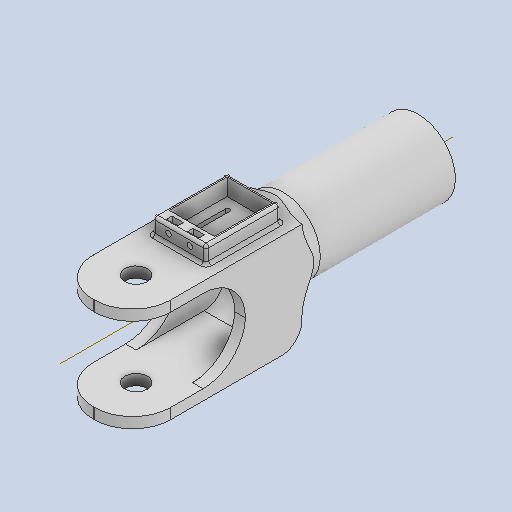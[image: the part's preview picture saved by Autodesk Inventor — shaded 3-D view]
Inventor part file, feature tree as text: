
AUTODESK INVENTOR PART (.ipt)
format: ipt  version: 2024 (Build 280153000, 153)  size: 337,920 bytes
history: native  units: mm
features: extrude x10, fillet x7, sketch x3, shell x1
ambient origin geometry x8: Origin, YZ Plane, XZ Plane, XY Plane, X Axis, Y Axis, Z Axis, Center Point
bodies: Solid1 (feature_tree)
feature tree (21):
  extrude  "Extrusion1"  Depth=30.0mm TaperAngle=0.0deg
  extrude  "Extrusion2"  Depth=47.5mm
  extrude  "Extrusion3"  Depth=14.25mm
  shell  "Shell1"  Thickness=80.0mm
  extrude  "Extrusion4"  Depth=14.25mm
  fillet  "Fillet2"  Radius=7.5mm
  extrude  "Extrusion5"  Depth=14.25mm
  fillet  "Fillet5"  Radius=80.0mm
  extrude  "Extrusion6"  Depth=14.25mm TaperAngle=0.0deg
  extrude  "Extrusion8"  Depth=14.25mm
  fillet  "Fillet6"  Radius=80.0mm
  extrude  "Extrusion9"  Depth=14.25mm
  extrude  "Extrusion10"  Depth=14.25mm
  extrude  "Extrusion11"  Depth=14.25mm
  fillet  "Fillet7"  Radius=46.0mm
  fillet  "Fillet8"  Radius=30.0mm
  fillet  "Fillet9"  Radius=55.0mm
  fillet  "Fillet10"  Radius=30.0mm
  sketch  "Sketch1"  dims[d1=52.629mm d2=30.0mm d3=0.0mm]
  sketch  "Sketch5"  dims[d6=47.5mm d7=47.5mm]
  sketch  "Sketch10"  dims[d9=120.0mm d10=0.0mm d12=52.629mm d13=80.0mm d14=0.0mm d15=7.5mm d16=7.5mm d17=7.5mm d18=80.0mm d19=80.0mm d20=0.0mm d21=27.0mm d22=80.0mm d23=0.0mm d24=55.0mm d25=27.5mm d26=27.5mm d27=46.0mm d30=30.0mm d31=55.0mm d32=30.0mm d33=16.0mm d34=0.0mm d35=0.0mm d41=3.0mm d42=3.0mm d43=12.0mm d44=6.0mm d45=28.0mm d46=16.0mm d47=20.0mm d48=0.0mm d49=1.5mm d51=16.0mm d52=8.0mm d53=8.0mm d54=3.0mm d55=12.0mm d56=0.0mm d59=53.0mm d60=14.426mm d61=60.0mm d62=6.0mm d63=4.0mm d64=4.5mm d65=4.5mm d66=3.5mm d67=3.5mm d68=8.0mm d69=8.0mm d70=7.0mm d71=0.0mm d72=4.0mm d73=4.0mm d74=19.0mm d76=7.5mm d77=7.0mm d78=0.0mm d79=2.0mm d80=14.25mm d81=14.25mm d82=14.25mm d83=5.5mm]
